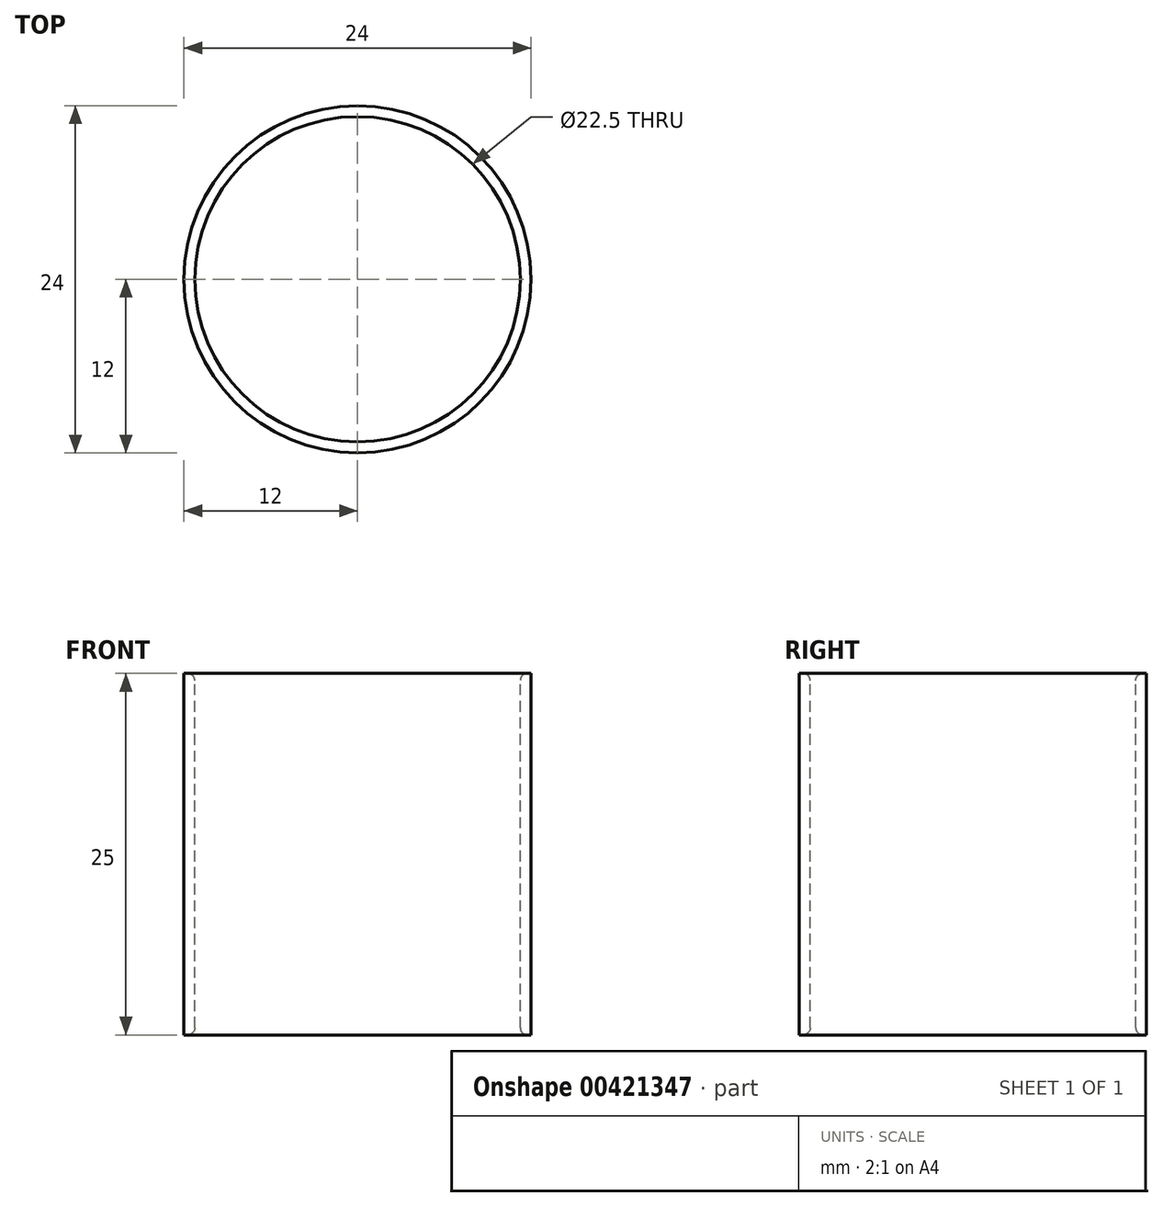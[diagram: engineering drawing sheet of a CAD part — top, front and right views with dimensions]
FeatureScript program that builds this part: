
annotation { "Feature Type Name" : "Feature", "Feature Type Description" : "" }
export const myFeature = defineFeature(function(context is Context, id is Id, definition is map)
    precondition{}
    {
        {
            var Q0;
            Q0=qCreatedBy(makeId("Top.planeOp"),FACE);
            var sketch = newSketch(context, id + "F0", { "sketchPlane" : qUnion([Q0])});
            skCircle(sketch, "E0", {"center": v(0, 0) * mm, "radius": 11.25 * mm});
            skCircle(sketch, "E1.0", {"center": v(0, 0) * mm, "radius": 12 * mm});
            skSolve(sketch);
        }
        {
            var Q0;
            Q0 = qSketchRegion(id + "F0", true);
            extrude(context, id + "F1", {"entities" : qUnion([Q0]), "oppositeDirection" : true, "depth" : 25 * mm});
        }
        {
            var Q0;
            Q0=makeQuery(id+"F1.opExtrude","CAP_EDGE",EDGE,{"disambiguationData":[OSD([sQuery(id+"F0.wireOp",EDGE,"E0")])],"isStart":false});
            var Q1;
            Q1=makeQuery(id+"F1.opExtrude","CAP_EDGE",EDGE,{"disambiguationData":[OSD([sQuery(id+"F0.wireOp",EDGE,"E0")])],"isStart":true});
            fillet(context, id + "F2", {"entities" : qUnion([Q0, Q1]), "radius" : .5 * mm, "tangentPropagation" : true, "allowEdgeOverflow" : false});
        }
    });
